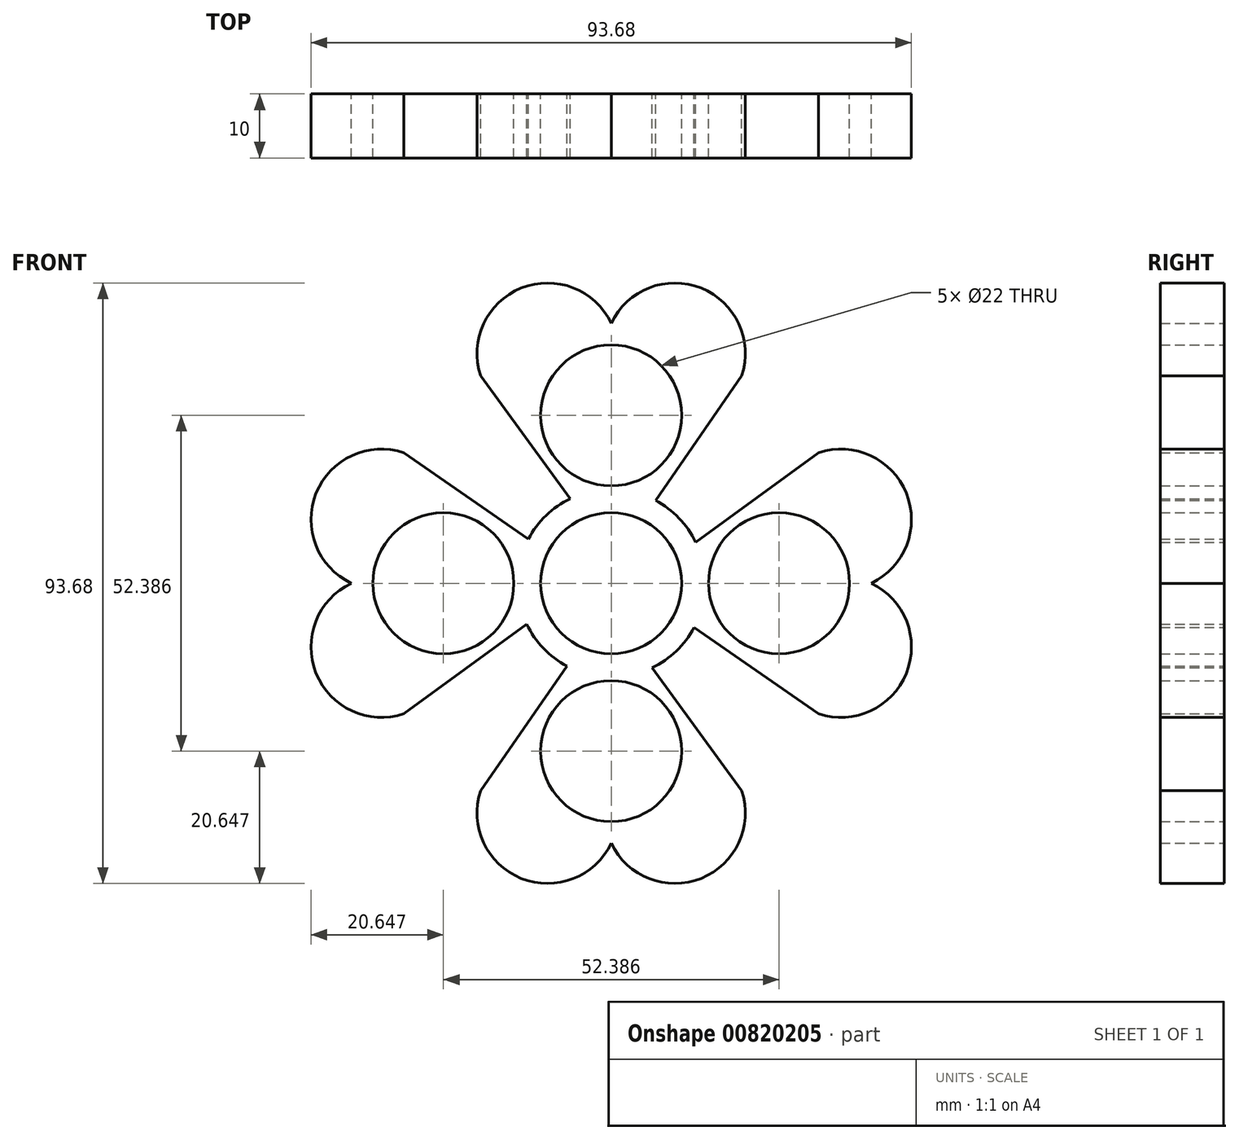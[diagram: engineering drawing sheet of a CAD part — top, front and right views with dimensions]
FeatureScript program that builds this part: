
annotation { "Feature Type Name" : "Feature", "Feature Type Description" : "" }
export const myFeature = defineFeature(function(context is Context, id is Id, definition is map)
    precondition{}
    {
        {
            var Q0;
            Q0=qCreatedBy(makeId("Front.planeOp"),FACE);
            var sketch = newSketch(context, id + "F0", { "sketchPlane" : qUnion([Q0])});
            skCircle(sketch, "E0", {"center": v(0, 26.2) * mm, "radius": 11 * mm});
            skLineSegment(sketch, "E1", {"start": v(-6.4, 13.19) * mm, "end": v(-20.37, 32.36) * mm});
            skArc(sketch, "E2", {"start": v(0, 40.57) * mm, "mid": v(-14.05, 46.05) * mm, "end": v(-20.37, 32.36) * mm});
            skArc(sketch, "E3.MirrorCS", {"start": v(0, 40.57) * mm, "mid": v(14.05, 46.05) * mm, "end": v(20.37, 32.36) * mm});
            skLineSegment(sketch, "E4", {"start": v(20.37, 32.36) * mm, "end": v(6.91, 12.92) * mm});
            skLineSegment(sketch, "E5.1.0", {"start": v(-32.36, 20.37) * mm, "end": v(-12.92, 6.91) * mm});
            skArc(sketch, "E5.1.1", {"start": v(-40.57, 0) * mm, "mid": v(-46.05, 14.05) * mm, "end": v(-32.36, 20.37) * mm});
            skArc(sketch, "E5.1.2", {"start": v(-40.57, 0) * mm, "mid": v(-46.05, -14.05) * mm, "end": v(-32.36, -20.37) * mm});
            skLineSegment(sketch, "E5.1.4", {"start": v(-13.19, -6.4) * mm, "end": v(-32.36, -20.37) * mm});
            skArc(sketch, "E5.1.5", {"start": v(-13.19, -6.4) * mm, "mid": v(-10.57, -10.16) * mm, "end": v(-6.91, -12.92) * mm});
            skCircle(sketch, "E5.1.6", {"center": v(-26.2, 0) * mm, "radius": 11 * mm});
            skCircle(sketch, "E5.1.7", {"center": v(0, 0) * mm, "radius": 11 * mm});
            skLineSegment(sketch, "E5.2.0", {"start": v(-20.37, -32.36) * mm, "end": v(-6.91, -12.92) * mm});
            skArc(sketch, "E5.2.1", {"start": v(0, -40.57) * mm, "mid": v(-14.05, -46.05) * mm, "end": v(-20.37, -32.36) * mm});
            skArc(sketch, "E5.2.2", {"start": v(0, -40.57) * mm, "mid": v(14.05, -46.05) * mm, "end": v(20.37, -32.36) * mm});
            skLineSegment(sketch, "E5.2.4", {"start": v(6.4, -13.19) * mm, "end": v(20.37, -32.36) * mm});
            skCircle(sketch, "E5.2.6", {"center": v(0, -26.2) * mm, "radius": 11 * mm});
            skLineSegment(sketch, "E5.3.0", {"start": v(32.36, -20.37) * mm, "end": v(12.92, -6.91) * mm});
            skArc(sketch, "E5.3.1", {"start": v(40.57, 0) * mm, "mid": v(46.05, -14.05) * mm, "end": v(32.36, -20.37) * mm});
            skArc(sketch, "E5.3.2", {"start": v(40.57, 0) * mm, "mid": v(46.05, 14.05) * mm, "end": v(32.36, 20.37) * mm});
            skLineSegment(sketch, "E5.3.4", {"start": v(13.19, 6.4) * mm, "end": v(32.36, 20.37) * mm});
            skArc(sketch, "E5.3.5", {"start": v(13.19, 6.4) * mm, "mid": v(10.57, 10.16) * mm, "end": v(6.91, 12.92) * mm});
            skCircle(sketch, "E5.3.6", {"center": v(26.2, 0) * mm, "radius": 11 * mm});
            skPoint(sketch, "E5.center", {"position": v(0, 0) * mm});
            skPoint(sketch, "E6.orphan", {"position": v(-54.9, 0) * mm});
            skArc(sketch, "E7.trimOffspring", {"start": v(6.4, -13.19) * mm, "mid": v(10.16, -10.57) * mm, "end": v(12.92, -6.91) * mm});
            skPoint(sketch, "E8.orphan", {"position": v(54.9, 0) * mm});
            skPoint(sketch, "E9.orphan", {"position": v(0, 54.9) * mm});
            skArc(sketch, "E10.trimOffspring", {"start": v(-6.4, 13.19) * mm, "mid": v(-10.16, 10.57) * mm, "end": v(-12.92, 6.91) * mm});
            skSolve(sketch);
        }
        {
            var Q0;
            Q0 = qSketchRegion(id + "F0", true);
            extrude(context, id + "F1", {"entities" : qUnion([Q0]), "depth" : 10 * mm, "offsetDistance" : 25 * mm});
        }
    });
